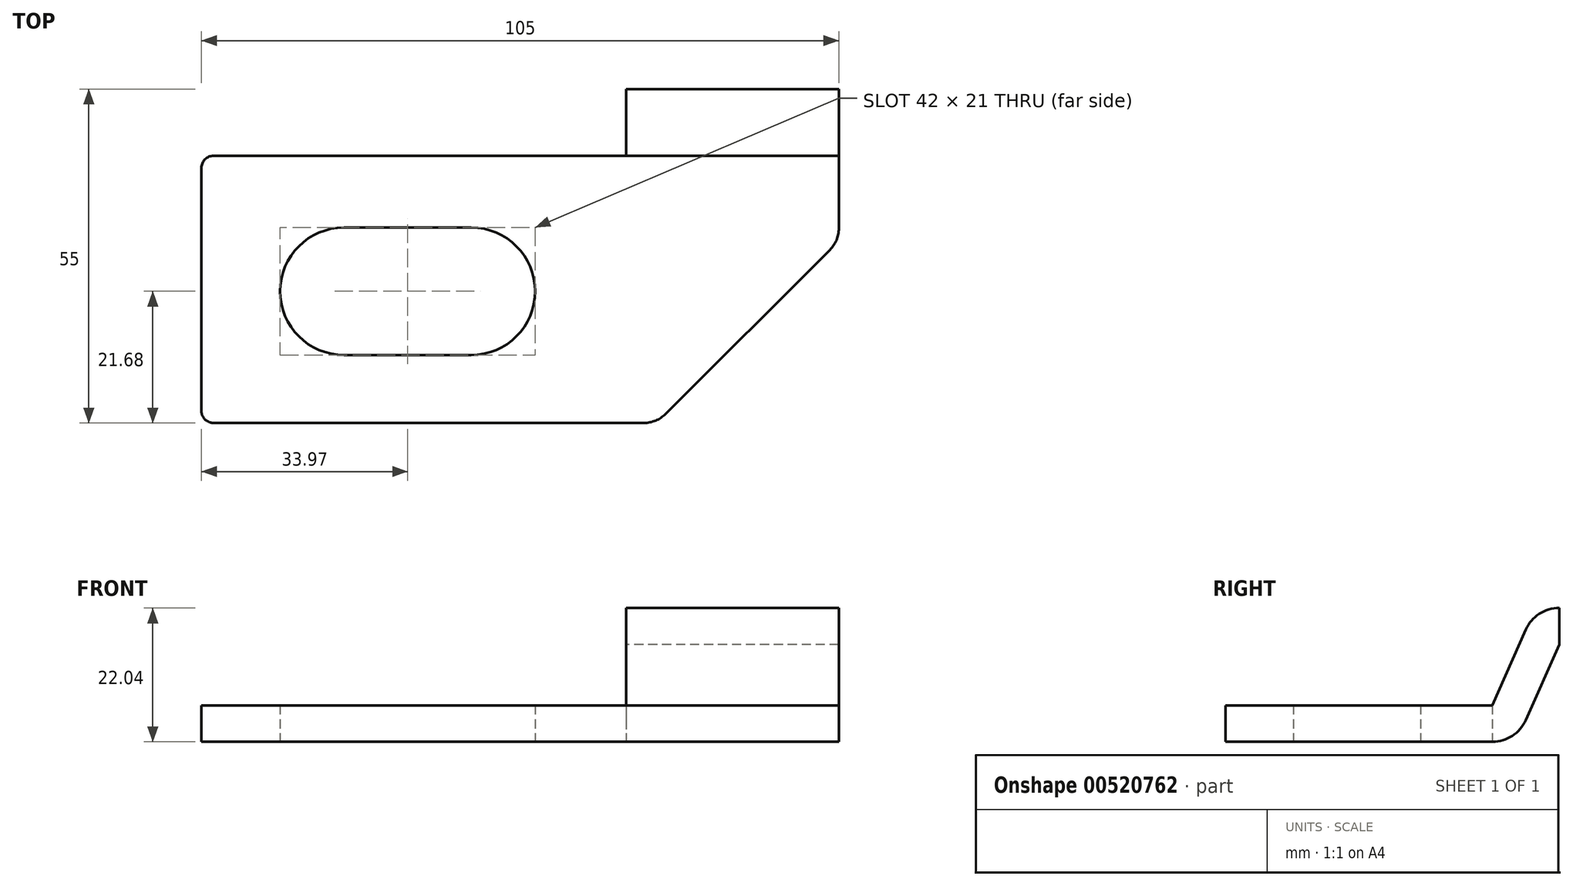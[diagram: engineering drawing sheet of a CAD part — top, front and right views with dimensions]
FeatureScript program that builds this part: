
annotation { "Feature Type Name" : "Feature", "Feature Type Description" : "" }
export const myFeature = defineFeature(function(context is Context, id is Id, definition is map)
    precondition{}
    {
        {
            var Q0;
            Q0=qCreatedBy(makeId("Top.planeOp"),FACE);
            var sketch = newSketch(context, id + "F0", { "sketchPlane" : qUnion([Q0])});
            skLineSegment(sketch, "E0.bottom", {"start": v(-52.1, -13.6) * mm, "end": v(50.9, -13.6) * mm});
            skLineSegment(sketch, "E0.top", {"start": v(-52.1, -57.6) * mm, "end": v(18.82, -57.6) * mm});
            skLineSegment(sketch, "E0.left", {"start": v(-54.1, -15.6) * mm, "end": v(-54.1, -55.6) * mm});
            skLineSegment(sketch, "E0.right", {"start": v(50.9, -13.6) * mm, "end": v(50.9, -25.57) * mm});
            skArc(sketch, "E1", {"start": v(-30.63, -25.42) * mm, "mid": v(-41.13, -35.92) * mm, "end": v(-30.63, -46.42) * mm});
            skArc(sketch, "E2", {"start": v(-9.63, -46.42) * mm, "mid": v(0.87, -35.92) * mm, "end": v(-9.63, -25.42) * mm});
            skLineSegment(sketch, "E3", {"start": v(-30.63, -25.42) * mm, "end": v(-9.63, -25.42) * mm});
            skLineSegment(sketch, "E4", {"start": v(-30.63, -46.42) * mm, "end": v(-9.63, -46.42) * mm});
            skLineSegment(sketch, "E5", {"start": v(-52.1, -13.6) * mm, "end": v(15.86, -13.6) * mm});
            skLineSegment(sketch, "E6", {"start": v(15.86, -13.6) * mm, "end": v(15.86, -2.6) * mm});
            skLineSegment(sketch, "E7", {"start": v(49.43, -29.1) * mm, "end": v(22.36, -56.14) * mm});
            skPoint(sketch, "E8.visualSharp", {"position": v(50.9, -27.64) * mm});
            skArc(sketch, "E8.filletArc", {"start": v(49.43, -29.1) * mm, "mid": v(50.52, -27.48) * mm, "end": v(50.9, -25.57) * mm});
            skPoint(sketch, "E9.visualSharp", {"position": v(20.9, -57.6) * mm});
            skArc(sketch, "E9.filletArc", {"start": v(18.82, -57.6) * mm, "mid": v(20.74, -57.22) * mm, "end": v(22.36, -56.14) * mm});
            skPoint(sketch, "E10.start.orphan", {"position": v(-54.1, -35.92) * mm});
            skLineSegment(sketch, "E11", {"start": v(50.9, -13.6) * mm, "end": v(50.9, -2.6) * mm});
            skLineSegment(sketch, "E12", {"start": v(15.86, -13.6) * mm, "end": v(50.9, -13.6) * mm});
            skLineSegment(sketch, "E13", {"start": v(-65.9, -57.6) * mm, "end": v(-65.9, -13.6) * mm});
            skLineSegment(sketch, "E14", {"start": v(-65.9, -13.6) * mm, "end": v(-83.58, 4.08) * mm});
            skLineSegment(sketch, "E15", {"start": v(-83.58, 4.08) * mm, "end": v(-83.58, 61.48) * mm});
            skPoint(sketch, "E16.visualSharp", {"position": v(-54.1, -57.6) * mm});
            skArc(sketch, "E16.filletArc", {"start": v(-54.1, -55.6) * mm, "mid": v(-53.51, -57.02) * mm, "end": v(-52.1, -57.6) * mm});
            skPoint(sketch, "E17.visualSharp", {"position": v(-54.1, -13.6) * mm});
            skArc(sketch, "E17.filletArc", {"start": v(-52.1, -13.6) * mm, "mid": v(-53.51, -14.19) * mm, "end": v(-54.1, -15.6) * mm});
            skLineSegment(sketch, "E18", {"start": v(-26.71, 36.6) * mm, "end": v(-26.71, 7.88) * mm});
            skArc(sketch, "E19.filletArc", {"start": v(-26.71, 7.88) * mm, "mid": v(-25.44, 4.55) * mm, "end": v(-22.28, 2.9) * mm});
            skLineSegment(sketch, "E20", {"start": v(24.38, 57.75) * mm, "end": v(-23.42, 41.29) * mm});
            skArc(sketch, "E21.filletArc", {"start": v(-23.42, 41.29) * mm, "mid": v(-25.8, 39.46) * mm, "end": v(-26.71, 36.6) * mm});
            skCircle(sketch, "E22", {"center": v(15.06, 11.28) * mm, "radius": 5 * mm});
            skArc(sketch, "E23", {"start": v(-19.71, 28.56) * mm, "mid": v(-16.37, 22.74) * mm, "end": v(-10.25, 25.5) * mm});
            skArc(sketch, "E24", {"start": v(-6.47, 31.29) * mm, "mid": v(-6.43, 38) * mm, "end": v(-13.1, 38.7) * mm});
            skArc(sketch, "E25", {"start": v(-13.1, 38.7) * mm, "mid": v(-17.34, 34.24) * mm, "end": v(-19.71, 28.56) * mm});
            skArc(sketch, "E26", {"start": v(-6.47, 31.29) * mm, "mid": v(-8.6, 28.54) * mm, "end": v(-10.25, 25.5) * mm});
            skCircle(sketch, "E27", {"center": v(32.85, 44.48) * mm, "radius": 3.5 * mm});
            skLineSegment(sketch, "E28", {"start": v(50.89, 38.84) * mm, "end": v(50.9, -2.6) * mm});
            skLineSegment(sketch, "E29.trimOffspring", {"start": v(-22.28, 2.9) * mm, "end": v(15.86, -2.6) * mm});
            skArc(sketch, "E30", {"start": v(50.89, 38.84) * mm, "mid": v(42.5, 55.12) * mm, "end": v(24.38, 57.75) * mm});
            skLineSegment(sketch, "E31", {"start": v(15.86, -2.6) * mm, "end": v(50.9, -2.6) * mm});
            skSolve(sketch);
        }
        {
            var Q0;
            Q0=makeQuery(id+"F0.imprint","IMPRINT",FACE,{"disambiguationData":[TD([[makeQuery(id+"F0.imprint","IMPRINT",EDGE,{"derivedFrom":sQuery(id+"F0.wireOp",EDGE,"8W7yfe0H-aZix-Sv96-F4wC-eh7qvSx2GVEx")}),1.0]])]});
            var Q1;
            {var subQ3=sQuery(id+"F0.wireOp",EDGE,"E6");Q1=makeQuery(id+"F0.imprint","IMPRINT",FACE,{"disambiguationData":[TD([[makeQuery(id+"F0.imprint","IMPRINT",EDGE,{"derivedFrom":subQ3}),-1.0]])]});}
            var Q2;
            {var subQ1=sQuery(id+"F0.wireOp",EDGE,"E0.left");Q2=makeQuery(id+"F0.imprint","IMPRINT",FACE,{"disambiguationData":[TD([[makeQuery(id+"F0.imprint","IMPRINT",EDGE,{"derivedFrom":subQ1}),1.0]])]});}
            var Q3;
            Q3 = qSketchRegion(id + "F2", true);
            extrude(context, id + "F1", {"entities" : qUnion([Q0, Q1, Q2, Q3]), "endBound" : BoundingType.SYMMETRIC, "depth" : 100 * mm, "offsetDistance" : 25 * mm});
        }
        {
            var Q0;
            Q0=qCreatedBy(makeId("Right.planeOp"),FACE);
            var sketch = newSketch(context, id + "F2", { "sketchPlane" : qUnion([Q0])});
            skLineSegment(sketch, "E32", {"start": v(-2.61, 31.44) * mm, "end": v(54.79, 31.44) * mm});
            skLineSegment(sketch, "E33", {"start": v(-57.6, 15.4) * mm, "end": v(-57.6, 21.4) * mm});
            skLineSegment(sketch, "E34", {"start": v(54.79, 37.46) * mm, "end": v(54.79, 31.44) * mm});
            skLineSegment(sketch, "E35", {"start": v(-2.61, 37.44) * mm, "end": v(54.79, 37.46) * mm});
            skArc(sketch, "E36", {"start": v(-2.61, 37.44) * mm, "mid": v(-2.61, 37.44) * mm, "end": v(-2.61, 37.44) * mm});
            skLineSegment(sketch, "E37", {"start": v(-13.6, 21.4) * mm, "end": v(-13.6, 15.4) * mm});
            skLineSegment(sketch, "E38", {"start": v(-2.61, 37.44) * mm, "end": v(-2.61, 31.44) * mm});
            skLineSegment(sketch, "E39", {"start": v(-13.6, 21.4) * mm, "end": v(-57.6, 21.4) * mm});
            skLineSegment(sketch, "E40", {"start": v(-13.6, 15.4) * mm, "end": v(-57.6, 15.4) * mm});
            skLineSegment(sketch, "E41", {"start": v(-2.61, 31.44) * mm, "end": v(-2.61, 37.44) * mm});
            skArc(sketch, "E42", {"start": v(-13.6, 15.4) * mm, "mid": v(-10.33, 16.37) * mm, "end": v(-8.12, 18.98) * mm});
            skArc(sketch, "E43", {"start": v(-2.61, 37.44) * mm, "mid": v(-5.89, 36.47) * mm, "end": v(-8.1, 33.87) * mm});
            skLineSegment(sketch, "E44", {"start": v(-8.1, 33.87) * mm, "end": v(-13.6, 21.4) * mm});
            skLineSegment(sketch, "E45", {"start": v(-8.12, 18.98) * mm, "end": v(-2.61, 31.44) * mm});
            skSolve(sketch);
        }
        {
            var Q0;
            Q0 = qSketchRegion(id + "F2", true);
            extrude(context, id + "F3", {"entities" : qUnion([Q0]), "endBound" : BoundingType.SYMMETRIC, "depth" : 250 * mm, "offsetDistance" : 25 * mm});
        }
        {
            var Q0;
            Q0=makeQuery(id+"F3.opExtrude","SWEPT_BODY",BODY,{"disambiguationData":[OSD([sQuery(id+"F2.wireOp",EDGE,"E32"),sQuery(id+"F2.wireOp",EDGE,"E33"),sQuery(id+"F2.wireOp",EDGE,"E34"),sQuery(id+"F2.wireOp",EDGE,"E35"),sQuery(id+"F2.wireOp",EDGE,"J25JDd9s-RQ6v-RNQd-7chh-Tqr3GTNpOswx"),sQuery(id+"F2.wireOp",EDGE,"E36"),sQuery(id+"F2.wireOp",EDGE,"r1x46NHF-3Qwy-ufdp-elit-wO6QNcAT7CoU"),sQuery(id+"F2.wireOp",EDGE,"prOrZiZI-Lg0r-eGxm-lJlR-tqgYX9q3gR2H"),sQuery(id+"F2.wireOp",EDGE,"E39"),sQuery(id+"F2.wireOp",EDGE,"E40")])]});
            var Q1;
            Q1=makeQuery(id+"F1.opExtrude","SWEPT_BODY",BODY,{"disambiguationData":[OSD([sQuery(id+"F0.wireOp",EDGE,"E0.left"),sQuery(id+"F0.wireOp",EDGE,"E0.right"),sQuery(id+"F0.wireOp",EDGE,"E1"),sQuery(id+"F0.wireOp",EDGE,"E2"),sQuery(id+"F0.wireOp",EDGE,"E3"),sQuery(id+"F0.wireOp",EDGE,"E4"),sQuery(id+"F0.wireOp",EDGE,"E5"),sQuery(id+"F0.wireOp",EDGE,"E6"),sQuery(id+"F0.wireOp",EDGE,"E0.top"),sQuery(id+"F0.wireOp",EDGE,"E7"),sQuery(id+"F0.wireOp",EDGE,"wPS2CQpd-gy8a-hakB-GyRP-7X7vxchye1ey"),sQuery(id+"F0.wireOp",EDGE,"4RxJgl4d-rHGj-E6fJ-J3Qt-Ho2dvTywX7QI"),sQuery(id+"F0.wireOp",EDGE,"412d9c70-411f-433e-a837-8ed45ec3a5ff.filletArc"),sQuery(id+"F0.wireOp",EDGE,"E8.filletArc"),sQuery(id+"F0.wireOp",EDGE,"VEYyszPP-Zapv-uYHJ-qWHW-2RddQyQjj8Qd"),sQuery(id+"F0.wireOp",EDGE,"a21c8da9-a600-4e57-a493-48099bde0555.filletArc"),sQuery(id+"F0.wireOp",EDGE,"E9.filletArc"),sQuery(id+"F0.wireOp",EDGE,"WVrtbWGg-C49i-esAu-y6rL-AwTZc30DX2eV"),sQuery(id+"F0.wireOp",EDGE,"d39d4709-d812-4df5-9805-aebb2c032c59"),sQuery(id+"F0.wireOp",EDGE,"520ab3ab-f6d8-41f2-9642-25b7d7dc8ce3"),sQuery(id+"F0.wireOp",EDGE,"ry6hx0Wl-Gks3-DKF9-qzgH-MmT10YdJ34V2"),sQuery(id+"F0.wireOp",EDGE,"6b538c2e-8186-4232-9525-548e96844709"),sQuery(id+"F0.wireOp",EDGE,"3Yn7eWZH-uqZj-aWEx-n81i-E1HNAXz07cVP"),sQuery(id+"F0.wireOp",EDGE,"1e39MreH-JOfK-JZPV-UDxB-KlRJIb1ogoXF"),sQuery(id+"F0.wireOp",EDGE,"jz4m1BSi-L7GN-ED7P-n1fS-aWuuLJdBRi93"),sQuery(id+"F0.wireOp",EDGE,"E11")])]});
            booleanBodies(context, id + "F4", {"operationType" : BooleanOperationType.INTERSECTION, "tools" : qUnion([Q0, Q1])});
        }
    });
